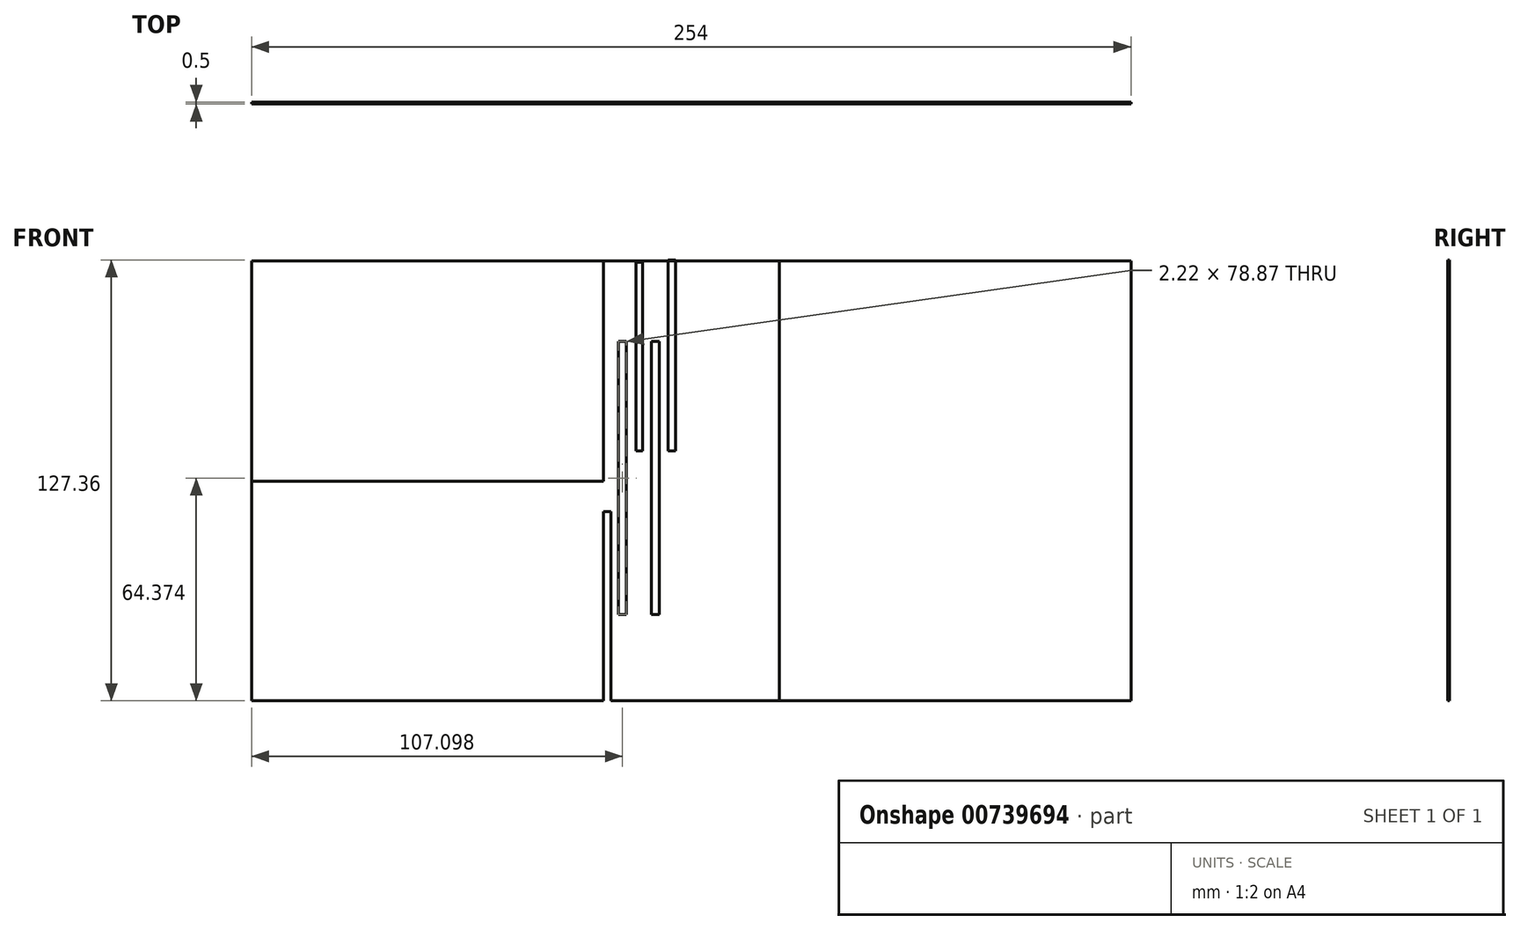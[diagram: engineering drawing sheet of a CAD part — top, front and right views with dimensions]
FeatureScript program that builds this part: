
annotation { "Feature Type Name" : "Feature", "Feature Type Description" : "" }
export const myFeature = defineFeature(function(context is Context, id is Id, definition is map)
    precondition{}
    {
        {
            var Q0;
            Q0=qCreatedBy(makeId("Front.planeOp"),FACE);
            var sketch = newSketch(context, id + "F0", { "sketchPlane" : qUnion([Q0])});
            skLineSegment(sketch, "E0.bottom", {"start": v(-128.63, 59.53) * mm, "end": v(-27.03, 59.53) * mm});
            skLineSegment(sketch, "E0.top", {"start": v(-128.63, -67.47) * mm, "end": v(-27.03, -67.47) * mm});
            skLineSegment(sketch, "E0.left", {"start": v(-128.63, 59.53) * mm, "end": v(-128.63, -67.47) * mm});
            skLineSegment(sketch, "E0.right", {"start": v(-27.03, 59.53) * mm, "end": v(-27.03, -67.47) * mm});
            skLineSegment(sketch, "E1", {"start": v(-27.03, 59.53) * mm, "end": v(23.77, 59.53) * mm});
            skLineSegment(sketch, "E2", {"start": v(-27.03, -67.47) * mm, "end": v(23.77, -67.47) * mm});
            skLineSegment(sketch, "E3.bottom", {"start": v(23.77, 59.53) * mm, "end": v(125.37, 59.53) * mm});
            skLineSegment(sketch, "E3.top", {"start": v(23.77, -67.47) * mm, "end": v(125.37, -67.47) * mm});
            skLineSegment(sketch, "E3.left", {"start": v(23.77, 59.53) * mm, "end": v(23.77, -67.47) * mm});
            skLineSegment(sketch, "E3.right", {"start": v(125.37, 59.53) * mm, "end": v(125.37, -67.47) * mm});
            skLineSegment(sketch, "E4", {"start": v(-27.03, 59.53) * mm, "end": v(-1.63, 59.53) * mm});
            skLineSegment(sketch, "E5", {"start": v(-128.63, 59.53) * mm, "end": v(-128.63, -3.97) * mm});
            skLineSegment(sketch, "E6.bottom", {"start": v(-128.63, 59.53) * mm, "end": v(-1.98, 59.53) * mm});
            skLineSegment(sketch, "E6.top", {"start": v(-128.63, -4) * mm, "end": v(-1.98, -4) * mm});
            skLineSegment(sketch, "E6.left", {"start": v(-128.63, 59.53) * mm, "end": v(-128.63, -4) * mm});
            skLineSegment(sketch, "E6.right", {"start": v(-1.98, 59.53) * mm, "end": v(-1.98, -4) * mm});
            skLineSegment(sketch, "E7.bottom", {"start": v(-27.03, -67.47) * mm, "end": v(-24.83, -67.47) * mm});
            skLineSegment(sketch, "E7.top", {"start": v(-27.03, -12.82) * mm, "end": v(-24.83, -12.82) * mm});
            skLineSegment(sketch, "E7.left", {"start": v(-27.03, -67.47) * mm, "end": v(-27.03, -12.82) * mm});
            skLineSegment(sketch, "E7.right", {"start": v(-24.83, -67.47) * mm, "end": v(-24.83, -12.82) * mm});
            skLineSegment(sketch, "E8.MirrorCS", {"start": v(-27.03, 4.8) * mm, "end": v(-24.83, 4.8) * mm});
            skLineSegment(sketch, "E9.MirrorCS", {"start": v(-27.03, 59.46) * mm, "end": v(-27.03, 4.8) * mm});
            skLineSegment(sketch, "E10.MirrorCS", {"start": v(-24.83, 59.46) * mm, "end": v(-24.83, 4.8) * mm});
            skLineSegment(sketch, "E11.bottom", {"start": v(-22.64, -42.53) * mm, "end": v(-20.42, -42.53) * mm});
            skLineSegment(sketch, "E11.top", {"start": v(-22.64, 36.34) * mm, "end": v(-20.42, 36.34) * mm});
            skLineSegment(sketch, "E11.left", {"start": v(-22.64, -42.53) * mm, "end": v(-22.64, 36.34) * mm});
            skLineSegment(sketch, "E11.right", {"start": v(-20.42, -42.53) * mm, "end": v(-20.42, 36.34) * mm});
            skSolve(sketch);
        }
        {
            var Q0;
            {var subQ6=sQuery(id+"F0.wireOp",EDGE,"E0.bottom");Q0=makeQuery(id+"F0.imprint","IMPRINT",FACE,{"disambiguationData":[TD([[makeQuery(id+"F0.imprint","IMPRINT",EDGE,{"derivedFrom":subQ6}),-1.0]])]});}
            var sketch = newSketch(context, id + "F1", { "sketchPlane" : qUnion([Q0])});
            skLineSegment(sketch, "E12.bottom", {"start": v(-17.59, -12.74) * mm, "end": v(-15.7, -12.74) * mm});
            skLineSegment(sketch, "E12.top", {"start": v(-17.59, -67.27) * mm, "end": v(-15.7, -67.27) * mm});
            skLineSegment(sketch, "E12.left", {"start": v(-17.59, -12.74) * mm, "end": v(-17.59, -67.27) * mm});
            skLineSegment(sketch, "E12.right", {"start": v(-15.7, -12.74) * mm, "end": v(-15.7, -67.27) * mm});
            skLineSegment(sketch, "E13.MirrorCS", {"start": v(-17.59, 4.73) * mm, "end": v(-15.7, 4.73) * mm});
            skLineSegment(sketch, "E14.MirrorCS", {"start": v(-17.59, 4.73) * mm, "end": v(-17.59, 59.26) * mm});
            skLineSegment(sketch, "E15.MirrorCS", {"start": v(-15.7, 4.73) * mm, "end": v(-15.7, 59.26) * mm});
            skLineSegment(sketch, "E16.MirrorCS", {"start": v(-17.59, 59.26) * mm, "end": v(-15.7, 59.26) * mm});
            skLineSegment(sketch, "E17.bottom", {"start": v(-13.12, 36.33) * mm, "end": v(-10.8, 36.33) * mm});
            skLineSegment(sketch, "E17.top", {"start": v(-13.12, -42.54) * mm, "end": v(-10.8, -42.54) * mm});
            skLineSegment(sketch, "E17.left", {"start": v(-13.12, 36.33) * mm, "end": v(-13.12, -42.54) * mm});
            skLineSegment(sketch, "E17.right", {"start": v(-10.8, 36.33) * mm, "end": v(-10.8, -42.54) * mm});
            skLineSegment(sketch, "E18.bottom", {"start": v(-8.37, -12.74) * mm, "end": v(-6.11, -12.74) * mm});
            skLineSegment(sketch, "E18.top", {"start": v(-8.37, -67.9) * mm, "end": v(-6.11, -67.9) * mm});
            skLineSegment(sketch, "E18.left", {"start": v(-8.37, -12.74) * mm, "end": v(-8.37, -67.9) * mm});
            skLineSegment(sketch, "E18.right", {"start": v(-6.11, -12.74) * mm, "end": v(-6.11, -67.9) * mm});
            skLineSegment(sketch, "E19.MirrorCS", {"start": v(-8.37, 4.73) * mm, "end": v(-8.37, 59.89) * mm});
            skLineSegment(sketch, "E20.MirrorCS", {"start": v(-6.11, 4.73) * mm, "end": v(-6.11, 59.89) * mm});
            skLineSegment(sketch, "E21.MirrorCS", {"start": v(-8.37, 59.89) * mm, "end": v(-6.11, 59.89) * mm});
            skLineSegment(sketch, "E22.MirrorCS", {"start": v(-8.37, 4.73) * mm, "end": v(-6.11, 4.73) * mm});
            skLineSegment(sketch, "E23.bottom", {"start": v(-3.66, 36.33) * mm, "end": v(0, 36.33) * mm});
            skLineSegment(sketch, "E23.top", {"start": v(-3.66, -42.54) * mm, "end": v(0, -42.54) * mm});
            skLineSegment(sketch, "E23.left", {"start": v(-3.66, 36.33) * mm, "end": v(-3.66, -42.54) * mm});
            skLineSegment(sketch, "E23.right", {"start": v(0, 36.33) * mm, "end": v(0, -42.54) * mm});
            skSolve(sketch);
        }
        {
            var Q0;
            Q0=makeQuery(id+"F0.imprint","IMPRINT",FACE,{"disambiguationData":[TD([[makeQuery(id+"F0.imprint","IMPRINT",EDGE,{"derivedFrom":sQuery(id+"F0.wireOp",EDGE,"E3.bottom")}),-1.0]])]});
            var sketch = newSketch(context, id + "F2", { "sketchPlane" : qUnion([Q0])});
            skLineSegment(sketch, "E24.top", {"start": v(2.77, -12.69) * mm, "end": v(5.18, -12.69) * mm});
            skLineSegment(sketch, "E24.left", {"start": v(2.77, -67.47) * mm, "end": v(2.77, -12.69) * mm});
            skLineSegment(sketch, "E24.right", {"start": v(5.18, -67.47) * mm, "end": v(5.18, -12.69) * mm});
            skLineSegment(sketch, "E25.MirrorCS", {"start": v(5.18, 59.46) * mm, "end": v(5.18, 4.67) * mm});
            skLineSegment(sketch, "E26.MirrorCS", {"start": v(2.77, 59.46) * mm, "end": v(2.77, 4.67) * mm});
            skLineSegment(sketch, "E27.MirrorCS", {"start": v(2.77, 4.67) * mm, "end": v(5.18, 4.67) * mm});
            skLineSegment(sketch, "E28.bottom", {"start": v(7.23, 36.44) * mm, "end": v(9.76, 36.44) * mm});
            skLineSegment(sketch, "E28.top", {"start": v(7.23, -42.58) * mm, "end": v(9.76, -42.58) * mm});
            skLineSegment(sketch, "E28.left", {"start": v(7.23, 36.44) * mm, "end": v(7.23, -42.58) * mm});
            skLineSegment(sketch, "E28.right", {"start": v(9.76, 36.44) * mm, "end": v(9.76, -42.58) * mm});
            skLineSegment(sketch, "E29.top", {"start": v(12.3, 4.8) * mm, "end": v(15.6, 4.8) * mm});
            skLineSegment(sketch, "E29.left", {"start": v(12.3, 59.52) * mm, "end": v(12.3, 4.8) * mm});
            skLineSegment(sketch, "E29.right", {"start": v(15.6, 59.52) * mm, "end": v(15.6, 4.8) * mm});
            skLineSegment(sketch, "E30.MirrorCS", {"start": v(12.3, -12.81) * mm, "end": v(15.6, -12.81) * mm});
            skLineSegment(sketch, "E31.MirrorCS", {"start": v(15.6, -67.53) * mm, "end": v(15.6, -12.81) * mm});
            skLineSegment(sketch, "E32.MirrorCS", {"start": v(12.3, -67.53) * mm, "end": v(12.3, -12.81) * mm});
            skLineSegment(sketch, "E33.bottom", {"start": v(18.5, 36.42) * mm, "end": v(21.7, 36.42) * mm});
            skLineSegment(sketch, "E33.top", {"start": v(18.5, -42.52) * mm, "end": v(21.7, -42.52) * mm});
            skLineSegment(sketch, "E33.left", {"start": v(18.5, 36.42) * mm, "end": v(18.5, -42.52) * mm});
            skLineSegment(sketch, "E33.right", {"start": v(21.7, 36.42) * mm, "end": v(21.7, -42.52) * mm});
            skPoint(sketch, "E34.MirrorCS.end.orphan", {"position": v(5.18, 59.46) * mm});
            skPoint(sketch, "E34.MirrorCS.start.orphan", {"position": v(2.77, 59.46) * mm});
            skSolve(sketch);
        }
        {
            var Q0;
            {var subQ6=sQuery(id+"F0.wireOp",EDGE,"E0.bottom");Q0=makeQuery(id+"F0.imprint","IMPRINT",FACE,{"disambiguationData":[TD([[makeQuery(id+"F0.imprint","IMPRINT",EDGE,{"derivedFrom":subQ6}),-1.0]])]});}
            var sketch = newSketch(context, id + "F3", { "sketchPlane" : qUnion([Q0])});
            skSolve(sketch);
        }
        {
            var Q0;
            {var subQ6=sQuery(id+"F0.wireOp",EDGE,"E0.bottom");Q0=makeQuery(id+"F3.imprint","IMPRINT",FACE,{"disambiguationData":[TD([[makeQuery(id+"F3.imprint","IMPRINT",EDGE,{"derivedFrom":makeQuery(id+"F0.imprint","IMPRINT",EDGE,{"derivedFrom":subQ6})}),-1.0]])]});}
            var Q1;
            {var subQ6=sQuery(id+"F0.wireOp",EDGE,"E0.top");Q1=makeQuery(id+"F0.imprint","IMPRINT",FACE,{"disambiguationData":[TD([[makeQuery(id+"F0.imprint","IMPRINT",EDGE,{"derivedFrom":subQ6}),1.0]])]});}
            var Q2;
            {var subQ5=sQuery(id+"F0.wireOp",EDGE,"E3.left");Q2=makeQuery(id+"F0.imprint","IMPRINT",FACE,{"disambiguationData":[TD([[makeQuery(id+"F0.imprint","IMPRINT",EDGE,{"derivedFrom":subQ5}),-1.0]])]});}
            var Q3;
            {var subQ3=sQuery(id+"F0.wireOp",EDGE,"E6.right");Q3=makeQuery(id+"F0.imprint","IMPRINT",FACE,{"disambiguationData":[TD([[makeQuery(id+"F0.imprint","IMPRINT",EDGE,{"derivedFrom":subQ3}),-1.0]])]});}
            var Q4;
            Q4=makeQuery(id+"F2.imprint","IMPRINT",FACE,{"disambiguationData":[TD([[makeQuery(id+"F2.imprint","IMPRINT",EDGE,{"derivedFrom":makeQuery(id+"F0.imprint","IMPRINT",EDGE,{"derivedFrom":sQuery(id+"F0.wireOp",EDGE,"E3.bottom")})}),-1.0]])]});
            var Q5;
            Q5=makeQuery(id+"F1.imprint","IMPRINT",FACE,{"disambiguationData":[TD([[makeQuery(id+"F1.imprint","IMPRINT",EDGE,{"derivedFrom":sQuery(id+"F1.wireOp",EDGE,"E13.MirrorCS")}),1.0]])]});
            var Q6;
            Q6=makeQuery(id+"F1.imprint","IMPRINT",FACE,{"disambiguationData":[TD([[makeQuery(id+"F1.imprint","IMPRINT",EDGE,{"derivedFrom":sQuery(id+"F1.wireOp",EDGE,"E17.bottom")}),-1.0]])]});
            var Q7;
            Q7=makeQuery(id+"F1.imprint","IMPRINT",FACE,{"disambiguationData":[TD([[makeQuery(id+"F1.imprint","IMPRINT",EDGE,{"derivedFrom":sQuery(id+"F1.wireOp",EDGE,"E19.MirrorCS")}),-1.0]])]});
            extrude(context, id + "F4", {"entities" : qUnion([Q0, Q1, Q2, Q3, Q4, Q5, Q6, Q7]), "depth" : .5 * mm, "offsetDistance" : 25 * mm});
        }
    });
